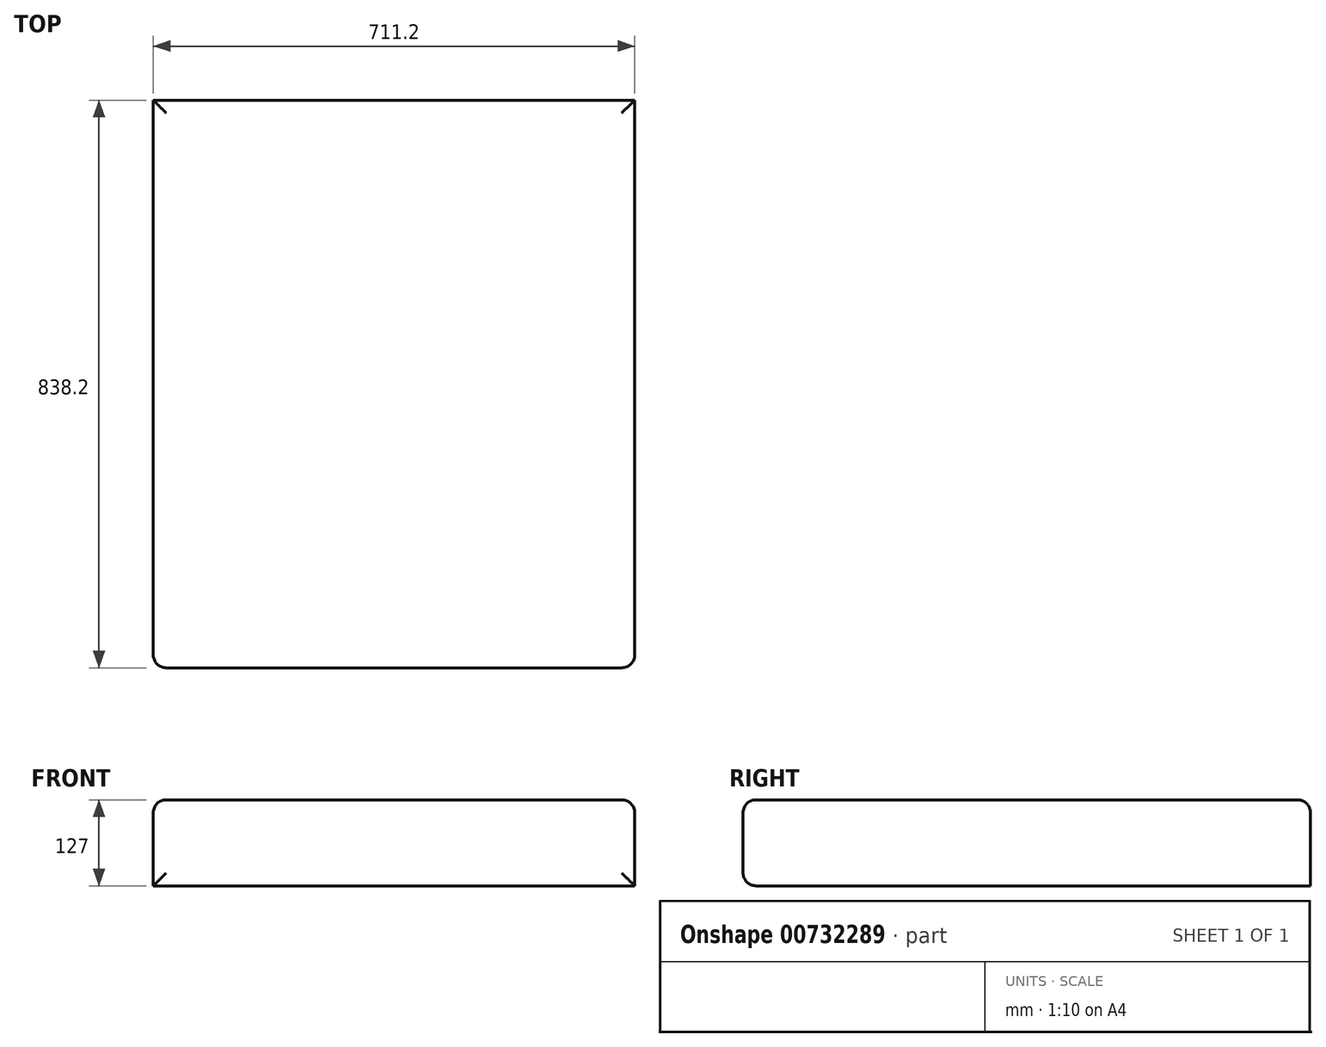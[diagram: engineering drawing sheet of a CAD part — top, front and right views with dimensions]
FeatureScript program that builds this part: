
annotation { "Feature Type Name" : "Feature", "Feature Type Description" : "" }
export const myFeature = defineFeature(function(context is Context, id is Id, definition is map)
    precondition{}
    {
        {
            var Q0;
            Q0=qCreatedBy(makeId("Top.planeOp"),FACE);
            var sketch = newSketch(context, id + "F0", { "sketchPlane" : qUnion([Q0])});
            skLineSegment(sketch, "E0.bottom", {"start": v(355.6, 419.1) * mm, "end": v(-355.6, 419.1) * mm});
            skLineSegment(sketch, "E0.top", {"start": v(355.6, -419.1) * mm, "end": v(-355.6, -419.1) * mm});
            skLineSegment(sketch, "E0.left", {"start": v(355.6, 419.1) * mm, "end": v(355.6, -419.1) * mm});
            skLineSegment(sketch, "E0.right", {"start": v(-355.6, 419.1) * mm, "end": v(-355.6, -419.1) * mm});
            skPoint(sketch, "E0.middle", {"position": v(0, 0) * mm});
            skSolve(sketch);
        }
        {
            var Q0;
            Q0=qSketchRegion(id+"F0",true);
            extrude(context, id + "F1", {"entities" : qUnion([Q0]), "depth" : 127 * mm, "offsetDistance" : 25.4 * mm});
        }
        {
            var Q0;
            Q0=makeQuery(id+"F1.opExtrude","CAP_EDGE",EDGE,{"disambiguationData":[OSD([sQuery(id+"F0.wireOp",EDGE,"E0.right")])],"isStart":false});
            var Q1;
            Q1=makeQuery(id+"F1.opExtrude","CAP_EDGE",EDGE,{"disambiguationData":[OSD([sQuery(id+"F0.wireOp",EDGE,"E0.top")])],"isStart":false});
            var Q2;
            Q2=makeQuery(id+"F1.opExtrude","CAP_EDGE",EDGE,{"disambiguationData":[OSD([sQuery(id+"F0.wireOp",EDGE,"E0.left")])],"isStart":false});
            var Q3;
            Q3=makeQuery(id+"F1.opExtrude","CAP_EDGE",EDGE,{"disambiguationData":[OSD([sQuery(id+"F0.wireOp",EDGE,"E0.bottom")])],"isStart":false});
            var Q4;
            Q4=makeQuery(id+"F1.opExtrude","CAP_EDGE",EDGE,{"disambiguationData":[OSD([sQuery(id+"F0.wireOp",EDGE,"E0.top")])],"isStart":true});
            var Q5;
            Q5=makeQuery(id+"F1.opExtrude","SWEPT_EDGE",EDGE,{"disambiguationData":[OSD([sQuery(id+"F0.wireOp",EDGE,"E0.top"),sQuery(id+"F0.wireOp",EDGE,"E0.left")])]});
            var Q6;
            Q6=makeQuery(id+"F1.opExtrude","SWEPT_EDGE",EDGE,{"disambiguationData":[OSD([sQuery(id+"F0.wireOp",EDGE,"E0.top"),sQuery(id+"F0.wireOp",EDGE,"E0.right")])]});
            fillet(context, id + "F2", {"entities" : qUnion([Q0, Q1, Q2, Q3, Q4, Q5, Q6]), "radius" : 19.05 * mm, "tangentPropagation" : true, "allowEdgeOverflow" : false});
        }
    });
